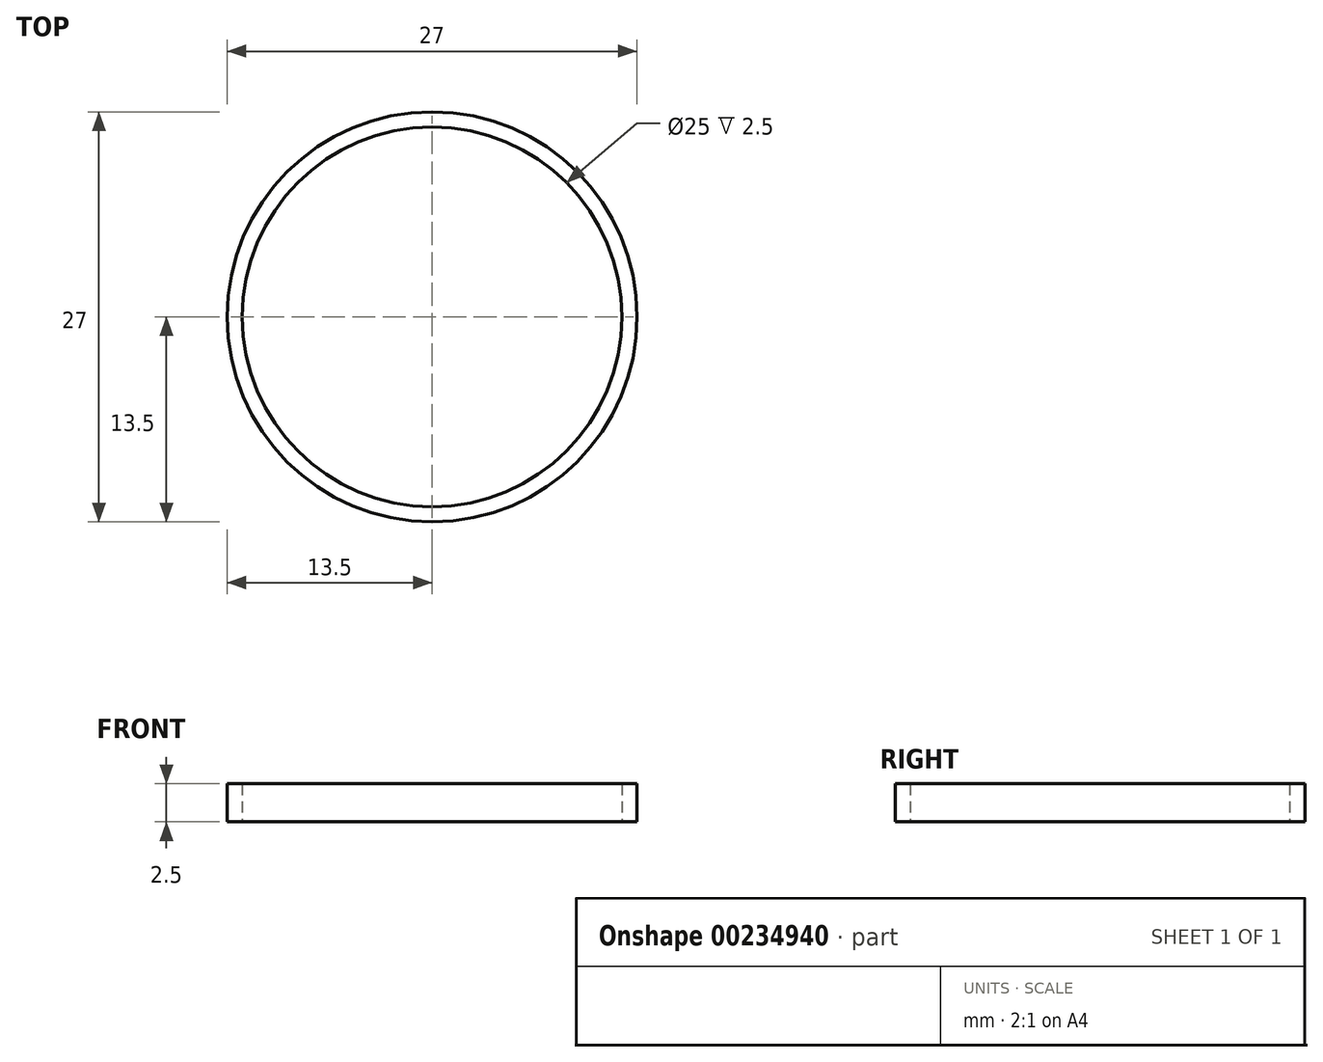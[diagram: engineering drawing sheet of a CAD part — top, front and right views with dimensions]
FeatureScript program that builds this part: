
annotation { "Feature Type Name" : "Feature", "Feature Type Description" : "" }
export const myFeature = defineFeature(function(context is Context, id is Id, definition is map)
    precondition{}
    {
        {
            var Q0;
            Q0=qCreatedBy(makeId("Top.planeOp"),FACE);
            var sketch = newSketch(context, id + "F0", { "sketchPlane" : qUnion([Q0])});
            skCircle(sketch, "E0", {"center": v(0, 0) * mm, "radius": 13.5 * mm});
            skCircle(sketch, "E1", {"center": v(0, 0) * mm, "radius": 12.5 * mm});
            skSolve(sketch);
        }
        {
            var Q0;
            Q0 = qSketchRegion(id + "F0", true);
            extrude(context, id + "F1", {"entities" : qUnion([Q0]), "depth" : 2.5 * mm});
        }
    });
